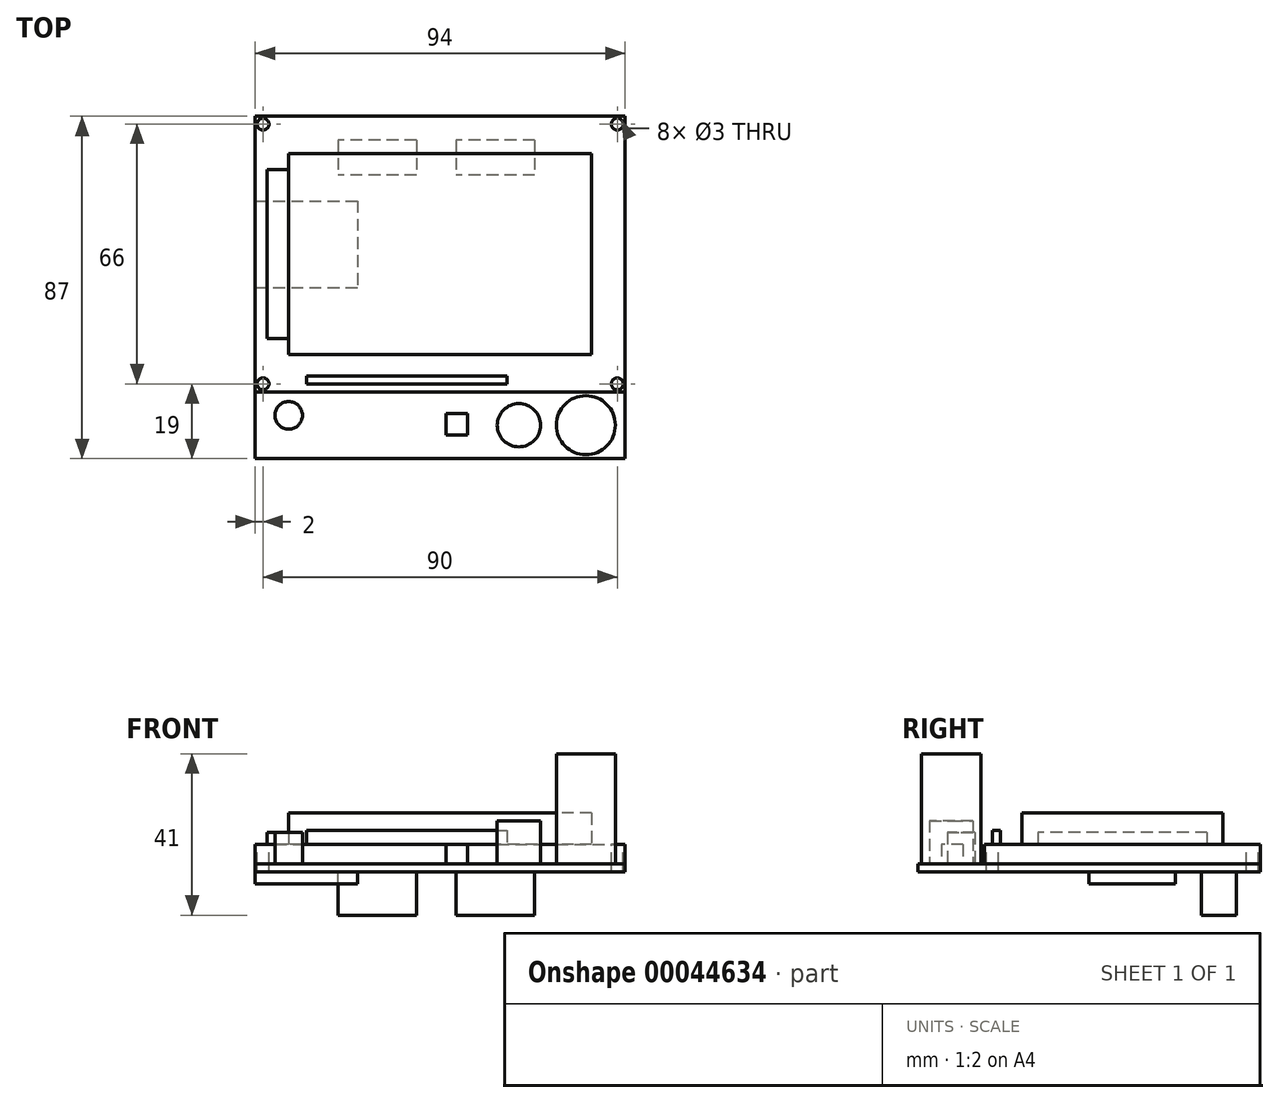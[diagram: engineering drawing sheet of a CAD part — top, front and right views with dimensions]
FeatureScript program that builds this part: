
annotation { "Feature Type Name" : "Feature", "Feature Type Description" : "" }
export const myFeature = defineFeature(function(context is Context, id is Id, definition is map)
    precondition{}
    {
        {
            var Q0;
            Q0=qCreatedBy(makeId("Top.planeOp"),FACE);
            var sketch = newSketch(context, id + "F0", { "sketchPlane" : qUnion([Q0])});
            skLineSegment(sketch, "E0.rect.bottom", {"start": v(47, 43.5) * mm, "end": v(-47, 43.5) * mm});
            skLineSegment(sketch, "E0.rect.top", {"start": v(47, -43.5) * mm, "end": v(-47, -43.5) * mm});
            skLineSegment(sketch, "E0.rect.left", {"start": v(47, 43.5) * mm, "end": v(47, -43.5) * mm});
            skLineSegment(sketch, "E0.rect.right", {"start": v(-47, 43.5) * mm, "end": v(-47, -43.5) * mm});
            skPoint(sketch, "E0.rect.middle", {"position": v(0, 0) * mm});
            skSolve(sketch);
        }
        {
            var Q0;
            Q0=makeQuery(id+"F0.imprint","IMPRINT",FACE,{"disambiguationData":[TD([[makeQuery(id+"F0.imprint","IMPRINT",EDGE,{"derivedFrom":sQuery(id+"F0.wireOp",EDGE,"E0.rect.bottom")}),1.0]])]});
            extrude(context, id + "F1", {"entities" : qUnion([Q0]), "depth" : 2 * mm});
        }
        {
            var Q0;
            Q0=makeQuery(id+"F1.opExtrude","CAP_FACE",FACE,{"disambiguationData":[OSD([sQuery(id+"F0.wireOp",EDGE,"E0.rect.bottom"),sQuery(id+"F0.wireOp",EDGE,"E0.rect.top"),sQuery(id+"F0.wireOp",EDGE,"E0.rect.left"),sQuery(id+"F0.wireOp",EDGE,"E0.rect.right")])],"isStart":false});
            var sketch = newSketch(context, id + "F2", { "sketchPlane" : qUnion([Q0])});
            skLineSegment(sketch, "E1.bottom", {"start": v(-47, 43.5) * mm, "end": v(47, 43.5) * mm});
            skLineSegment(sketch, "E1.top", {"start": v(-47, -26.5) * mm, "end": v(47, -26.5) * mm});
            skLineSegment(sketch, "E1.left", {"start": v(-47, 43.5) * mm, "end": v(-47, -26.5) * mm});
            skLineSegment(sketch, "E1.right", {"start": v(47, 43.5) * mm, "end": v(47, -26.5) * mm});
            skSolve(sketch);
        }
        {
            var Q0;
            Q0=makeQuery(id+"F2.imprint","IMPRINT",FACE,{"disambiguationData":[TD([[makeQuery(id+"F2.imprint","IMPRINT",EDGE,{"derivedFrom":sQuery(id+"F2.wireOp",EDGE,"E1.bottom")}),1.0]])]});
            extrude(context, id + "F3", {"entities" : qUnion([Q0]), "depth" : 5 * mm});
        }
        {
            var Q0;
            Q0=makeQuery(id+"F3.opExtrude","CAP_FACE",FACE,{"disambiguationData":[OSD([sQuery(id+"F2.wireOp",EDGE,"E1.bottom"),sQuery(id+"F2.wireOp",EDGE,"E1.top"),sQuery(id+"F2.wireOp",EDGE,"E1.left"),sQuery(id+"F2.wireOp",EDGE,"E1.right")])],"isStart":false});
            var sketch = newSketch(context, id + "F4", { "sketchPlane" : qUnion([Q0])});
            skLineSegment(sketch, "E2.rect.bottom", {"start": v(38.5, 34) * mm, "end": v(-38.5, 34) * mm});
            skLineSegment(sketch, "E2.rect.top", {"start": v(38.5, -17) * mm, "end": v(-38.5, -17) * mm});
            skLineSegment(sketch, "E2.rect.left", {"start": v(38.5, 34) * mm, "end": v(38.5, -17) * mm});
            skLineSegment(sketch, "E2.rect.right", {"start": v(-38.5, 34) * mm, "end": v(-38.5, -17) * mm});
            skPoint(sketch, "E2.rect.middle", {"position": v(0, 8.5) * mm});
            skSolve(sketch);
        }
        {
            var Q0;
            Q0=makeQuery(id+"F4.imprint","IMPRINT",FACE,{"disambiguationData":[TD([[makeQuery(id+"F4.imprint","IMPRINT",EDGE,{"derivedFrom":sQuery(id+"F4.wireOp",EDGE,"E2.rect.bottom")}),1.0]])]});
            extrude(context, id + "F5", {"entities" : qUnion([Q0]), "depth" : 8 * mm});
        }
        {
            var Q0;
            Q0=makeQuery(id+"F3.opExtrude","CAP_FACE",FACE,{"disambiguationData":[OSD([sQuery(id+"F2.wireOp",EDGE,"E1.bottom"),sQuery(id+"F2.wireOp",EDGE,"E1.top"),sQuery(id+"F2.wireOp",EDGE,"E1.left"),sQuery(id+"F2.wireOp",EDGE,"E1.right")])],"isStart":false});
            var sketch = newSketch(context, id + "F6", { "sketchPlane" : qUnion([Q0])});
            skLineSegment(sketch, "E3.bottom", {"start": v(-38.5, 30) * mm, "end": v(-44, 30) * mm});
            skLineSegment(sketch, "E3.top", {"start": v(-38.5, -13) * mm, "end": v(-44, -13) * mm});
            skLineSegment(sketch, "E3.left", {"start": v(-38.5, 30) * mm, "end": v(-38.5, -13) * mm});
            skLineSegment(sketch, "E3.right", {"start": v(-44, 30) * mm, "end": v(-44, -13) * mm});
            skSolve(sketch);
        }
        {
            var Q0;
            Q0=makeQuery(id+"F6.imprint","IMPRINT",FACE,{"disambiguationData":[TD([[makeQuery(id+"F6.imprint","IMPRINT",EDGE,{"derivedFrom":sQuery(id+"F6.wireOp",EDGE,"E3.bottom")}),1.0]])]});
            extrude(context, id + "F7", {"entities" : qUnion([Q0]), "depth" : 3 * mm});
        }
        {
            var Q0;
            Q0=makeQuery(id+"F1.opExtrude","CAP_FACE",FACE,{"disambiguationData":[OSD([sQuery(id+"F0.wireOp",EDGE,"E0.rect.bottom"),sQuery(id+"F0.wireOp",EDGE,"E0.rect.top"),sQuery(id+"F0.wireOp",EDGE,"E0.rect.left"),sQuery(id+"F0.wireOp",EDGE,"E0.rect.right")])],"isStart":false});
            var sketch = newSketch(context, id + "F8", { "sketchPlane" : qUnion([Q0])});
            skCircle(sketch, "E4", {"center": v(37, -35) * mm, "radius": 7.5 * mm});
            skSolve(sketch);
        }
        {
            var Q0;
            Q0=makeQuery(id+"F8.imprint","IMPRINT",FACE,{"disambiguationData":[TD([[makeQuery(id+"F8.imprint","IMPRINT",EDGE,{"derivedFrom":sQuery(id+"F8.wireOp",EDGE,"E4")}),1.0]])]});
            extrude(context, id + "F9", {"entities" : qUnion([Q0]), "depth" : 28 * mm});
        }
        {
            var Q0;
            Q0=makeQuery(id+"F1.opExtrude","CAP_FACE",FACE,{"disambiguationData":[OSD([sQuery(id+"F0.wireOp",EDGE,"E0.rect.bottom"),sQuery(id+"F0.wireOp",EDGE,"E0.rect.top"),sQuery(id+"F0.wireOp",EDGE,"E0.rect.left"),sQuery(id+"F0.wireOp",EDGE,"E0.rect.right")])],"isStart":false});
            var sketch = newSketch(context, id + "F10", { "sketchPlane" : qUnion([Q0])});
            skCircle(sketch, "E5", {"center": v(20, -35) * mm, "radius": 5.5 * mm});
            skSolve(sketch);
        }
        {
            var Q0;
            Q0=makeQuery(id+"F10.imprint","IMPRINT",FACE,{"disambiguationData":[TD([[makeQuery(id+"F10.imprint","IMPRINT",EDGE,{"derivedFrom":sQuery(id+"F10.wireOp",EDGE,"E5")}),1.0]])]});
            extrude(context, id + "F11", {"entities" : qUnion([Q0]), "depth" : 11 * mm});
        }
        {
            var Q0;
            Q0=makeQuery(id+"F1.opExtrude","CAP_FACE",FACE,{"disambiguationData":[OSD([sQuery(id+"F0.wireOp",EDGE,"E0.rect.bottom"),sQuery(id+"F0.wireOp",EDGE,"E0.rect.top"),sQuery(id+"F0.wireOp",EDGE,"E0.rect.left"),sQuery(id+"F0.wireOp",EDGE,"E0.rect.right")])],"isStart":false});
            var sketch = newSketch(context, id + "F12", { "sketchPlane" : qUnion([Q0])});
            skLineSegment(sketch, "E6.bottom", {"start": v(7, -32) * mm, "end": v(1.5, -32) * mm});
            skLineSegment(sketch, "E6.top", {"start": v(7, -37.5) * mm, "end": v(1.5, -37.5) * mm});
            skLineSegment(sketch, "E6.left", {"start": v(7, -32) * mm, "end": v(7, -37.5) * mm});
            skLineSegment(sketch, "E6.right", {"start": v(1.5, -32) * mm, "end": v(1.5, -37.5) * mm});
            skSolve(sketch);
        }
        {
            var Q0;
            Q0=makeQuery(id+"F12.imprint","IMPRINT",FACE,{"disambiguationData":[TD([[makeQuery(id+"F12.imprint","IMPRINT",EDGE,{"derivedFrom":sQuery(id+"F12.wireOp",EDGE,"E6.bottom")}),1.0]])]});
            extrude(context, id + "F13", {"entities" : qUnion([Q0]), "depth" : 5 * mm});
        }
        {
            var Q0;
            Q0=makeQuery(id+"F1.opExtrude","CAP_FACE",FACE,{"disambiguationData":[OSD([sQuery(id+"F0.wireOp",EDGE,"E0.rect.bottom"),sQuery(id+"F0.wireOp",EDGE,"E0.rect.top"),sQuery(id+"F0.wireOp",EDGE,"E0.rect.left"),sQuery(id+"F0.wireOp",EDGE,"E0.rect.right")])],"isStart":false});
            var sketch = newSketch(context, id + "F14", { "sketchPlane" : qUnion([Q0])});
            skCircle(sketch, "E7", {"center": v(-38.5, -32.5) * mm, "radius": 3.5 * mm});
            skSolve(sketch);
        }
        {
            var Q0;
            Q0=makeQuery(id+"F14.imprint","IMPRINT",FACE,{"disambiguationData":[TD([[makeQuery(id+"F14.imprint","IMPRINT",EDGE,{"derivedFrom":sQuery(id+"F14.wireOp",EDGE,"E7")}),1.0]])]});
            extrude(context, id + "F15", {"entities" : qUnion([Q0]), "depth" : 8 * mm});
        }
        {
            var Q0;
            Q0=makeQuery(id+"F3.opExtrude","CAP_FACE",FACE,{"disambiguationData":[OSD([sQuery(id+"F2.wireOp",EDGE,"E1.bottom"),sQuery(id+"F2.wireOp",EDGE,"E1.top"),sQuery(id+"F2.wireOp",EDGE,"E1.left"),sQuery(id+"F2.wireOp",EDGE,"E1.right")])],"isStart":false});
            var sketch = newSketch(context, id + "F16", { "sketchPlane" : qUnion([Q0])});
            skPoint(sketch, "E8", {"position": v(-45, 41.5) * mm});
            skPoint(sketch, "E9.MirrorP", {"position": v(45, 41.5) * mm});
            skPoint(sketch, "E10", {"position": v(45, -24.5) * mm});
            skPoint(sketch, "E11", {"position": v(-45, -24.5) * mm});
            skSolve(sketch);
        }
        {
            var Q0;
            Q0=sQuery(id+"F16.wireOp",VERTEX,"E8");
            var Q1;
            Q1=makeQuery(id+"F3.opExtrude","SWEPT_BODY",BODY,{"disambiguationData":[OSD([sQuery(id+"F2.wireOp",EDGE,"E1.bottom"),sQuery(id+"F2.wireOp",EDGE,"E1.top"),sQuery(id+"F2.wireOp",EDGE,"E1.left"),sQuery(id+"F2.wireOp",EDGE,"E1.right")])]});
            var Q2;
            Q2=makeQuery(id+"F1.opExtrude","SWEPT_BODY",BODY,{"disambiguationData":[OSD([sQuery(id+"F0.wireOp",EDGE,"E0.rect.bottom"),sQuery(id+"F0.wireOp",EDGE,"E0.rect.top"),sQuery(id+"F0.wireOp",EDGE,"E0.rect.left"),sQuery(id+"F0.wireOp",EDGE,"E0.rect.right")])]});
            hole(context, id + "F17", {"style" : HoleStyle.SIMPLE, "holeDiameter" : 3 * mm, "endStyle" : HoleEndStyle.BLIND, "holeDepth" : 20 * mm, "locations" : qUnion([Q0]), "scope" : qUnion([Q1, Q2])});
        }
        {
            var Q0;
            Q0=sQuery(id+"F16.wireOp",VERTEX,"E9.MirrorP");
            var Q1;
            Q1=sQuery(id+"F16.wireOp",VERTEX,"E10");
            var Q2;
            Q2=sQuery(id+"F16.wireOp",VERTEX,"E11");
            var Q3;
            Q3=makeQuery(id+"F3.opExtrude","SWEPT_BODY",BODY,{"disambiguationData":[OSD([sQuery(id+"F2.wireOp",EDGE,"E1.bottom"),sQuery(id+"F2.wireOp",EDGE,"E1.top"),sQuery(id+"F2.wireOp",EDGE,"E1.left"),sQuery(id+"F2.wireOp",EDGE,"E1.right")])]});
            var Q4;
            Q4=makeQuery(id+"F1.opExtrude","SWEPT_BODY",BODY,{"disambiguationData":[OSD([sQuery(id+"F0.wireOp",EDGE,"E0.rect.bottom"),sQuery(id+"F0.wireOp",EDGE,"E0.rect.top"),sQuery(id+"F0.wireOp",EDGE,"E0.rect.left"),sQuery(id+"F0.wireOp",EDGE,"E0.rect.right")])]});
            hole(context, id + "F18", {"style" : HoleStyle.SIMPLE, "holeDiameter" : 3 * mm, "endStyle" : HoleEndStyle.THROUGH, "locations" : qUnion([Q0, Q1, Q2]), "scope" : qUnion([Q3, Q4])});
        }
        {
            var Q0;
            Q0=makeQuery(id+"F16.imprint","IMPRINT",FACE,{"disambiguationData":[TD([[makeQuery(id+"F16.imprint","IMPRINT",EDGE,{"derivedFrom":makeQuery(id+"F3.opExtrude","CAP_EDGE",EDGE,{"disambiguationData":[OSD([sQuery(id+"F2.wireOp",EDGE,"E1.bottom")])],"isStart":false})}),1.0]])]});
            var sketch = newSketch(context, id + "F19", { "sketchPlane" : qUnion([Q0])});
            skLineSegment(sketch, "E12.bottom", {"start": v(-34, -24.5) * mm, "end": v(17, -24.5) * mm});
            skLineSegment(sketch, "E12.top", {"start": v(-34, -22.5) * mm, "end": v(17, -22.5) * mm});
            skLineSegment(sketch, "E12.left", {"start": v(-34, -24.5) * mm, "end": v(-34, -22.5) * mm});
            skLineSegment(sketch, "E12.right", {"start": v(17, -24.5) * mm, "end": v(17, -22.5) * mm});
            skSolve(sketch);
        }
        {
            var Q0;
            Q0=makeQuery(id+"F19.imprint","IMPRINT",FACE,{"disambiguationData":[TD([[makeQuery(id+"F19.imprint","IMPRINT",EDGE,{"derivedFrom":sQuery(id+"F19.wireOp",EDGE,"E12.bottom")}),1.0]])]});
            extrude(context, id + "F20", {"entities" : qUnion([Q0]), "depth" : 3.5 * mm});
        }
        {
            var Q0;
            Q0=makeQuery(id+"F1.opExtrude","CAP_FACE",FACE,{"disambiguationData":[OSD([sQuery(id+"F0.wireOp",EDGE,"E0.rect.bottom"),sQuery(id+"F0.wireOp",EDGE,"E0.rect.top"),sQuery(id+"F0.wireOp",EDGE,"E0.rect.left"),sQuery(id+"F0.wireOp",EDGE,"E0.rect.right")])],"isStart":true});
            var sketch = newSketch(context, id + "F21", { "sketchPlane" : qUnion([Q0])});
            skLineSegment(sketch, "E13.bottom", {"start": v(-47, -22) * mm, "end": v(-21, -22) * mm});
            skLineSegment(sketch, "E13.top", {"start": v(-47, 0) * mm, "end": v(-21, 0) * mm});
            skLineSegment(sketch, "E13.left", {"start": v(-47, -22) * mm, "end": v(-47, 0) * mm});
            skLineSegment(sketch, "E13.right", {"start": v(-21, -22) * mm, "end": v(-21, 0) * mm});
            skSolve(sketch);
        }
        {
            var Q0;
            Q0=makeQuery(id+"F21.imprint","IMPRINT",FACE,{"disambiguationData":[TD([[makeQuery(id+"F21.imprint","IMPRINT",EDGE,{"derivedFrom":sQuery(id+"F21.wireOp",EDGE,"E13.bottom")}),1.0]])]});
            extrude(context, id + "F22", {"entities" : qUnion([Q0]), "operationType" : NewBodyOperationType.ADD, "depth" : 3 * mm});
        }
        {
            var Q0;
            Q0=makeQuery(id+"F1.opExtrude","CAP_FACE",FACE,{"disambiguationData":[OSD([sQuery(id+"F0.wireOp",EDGE,"E0.rect.bottom"),sQuery(id+"F0.wireOp",EDGE,"E0.rect.top"),sQuery(id+"F0.wireOp",EDGE,"E0.rect.left"),sQuery(id+"F0.wireOp",EDGE,"E0.rect.right")])],"isStart":true});
            var sketch = newSketch(context, id + "F23", { "sketchPlane" : qUnion([Q0])});
            skLineSegment(sketch, "E14.bottom", {"start": v(24, -37.5) * mm, "end": v(4, -37.5) * mm});
            skLineSegment(sketch, "E14.top", {"start": v(24, -28.5) * mm, "end": v(4, -28.5) * mm});
            skLineSegment(sketch, "E14.left", {"start": v(24, -37.5) * mm, "end": v(24, -28.5) * mm});
            skLineSegment(sketch, "E14.right", {"start": v(4, -37.5) * mm, "end": v(4, -28.5) * mm});
            skLineSegment(sketch, "E15.bottom", {"start": v(-6, -37.5) * mm, "end": v(-26, -37.5) * mm});
            skLineSegment(sketch, "E15.top", {"start": v(-6, -28.5) * mm, "end": v(-26, -28.5) * mm});
            skLineSegment(sketch, "E15.left", {"start": v(-6, -37.5) * mm, "end": v(-6, -28.5) * mm});
            skLineSegment(sketch, "E15.right", {"start": v(-26, -37.5) * mm, "end": v(-26, -28.5) * mm});
            skSolve(sketch);
        }
        {
            var Q0;
            Q0=qSketchRegion(id+"F23",true);
            extrude(context, id + "F24", {"entities" : qUnion([Q0]), "operationType" : NewBodyOperationType.ADD, "depth" : 11 * mm});
        }
    });
